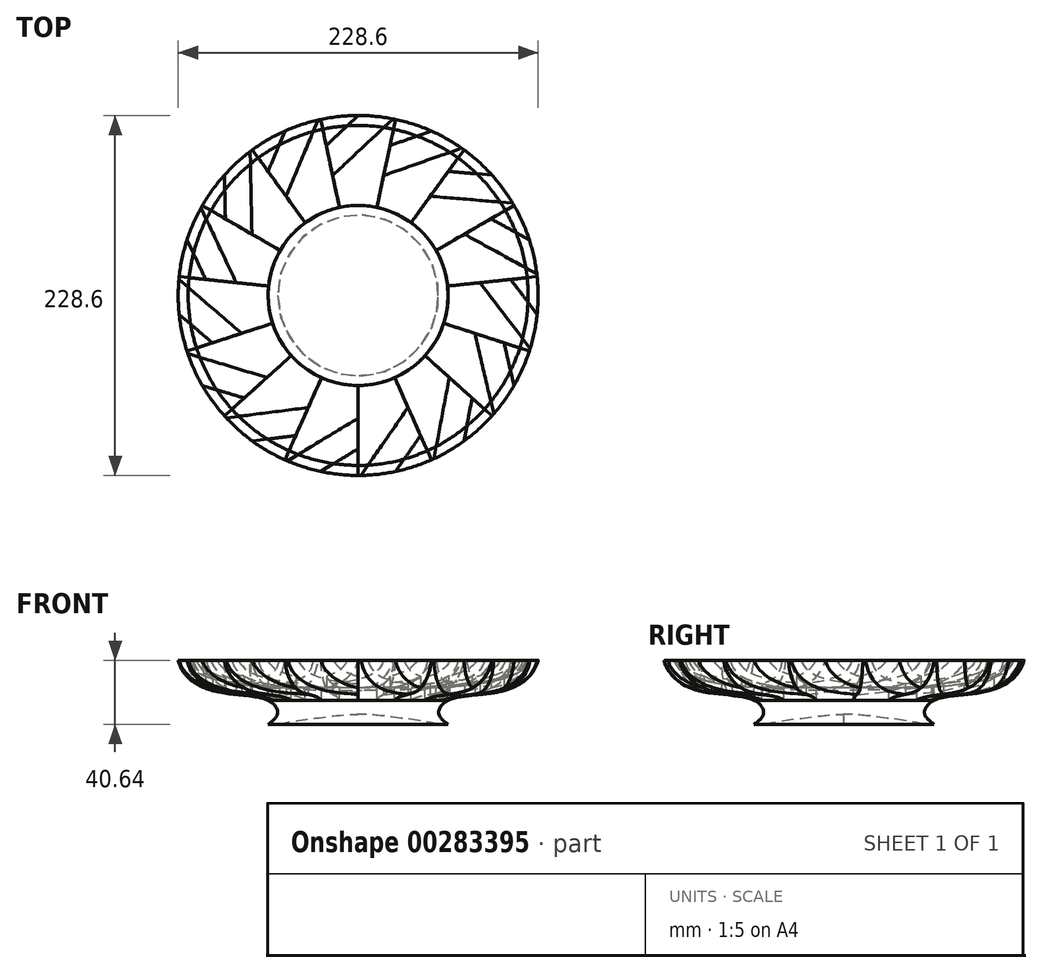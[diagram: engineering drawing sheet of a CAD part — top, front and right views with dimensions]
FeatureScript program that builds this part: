
annotation { "Feature Type Name" : "Feature", "Feature Type Description" : "" }
export const myFeature = defineFeature(function(context is Context, id is Id, definition is map)
    precondition{}
    {
        {
            var Q0;
            Q0=qCreatedBy(makeId("Top.planeOp"),FACE);
            var sketch = newSketch(context, id + "F0", { "sketchPlane" : qUnion([Q0])});
            skCircle(sketch, "E0", {"center": v(0, 0) * mm, "radius": 57.15 * mm});
            skLineSegment(sketch, "E1", {"start": v(0, 0) * mm, "end": v(0, 38.1) * mm, "construction": true});
            skLineSegment(sketch, "E2", {"start": v(0, 38.1) * mm, "end": v(0, 114.3) * mm, "construction": true});
            skCircle(sketch, "E3.cCircle", {"center": v(0, 0) * mm, "radius": 114.3 * mm, "construction": true});
            skLineSegment(sketch, "E3.0", {"start": v(-24.3, 114.3) * mm, "end": v(24.3, 114.3) * mm});
            skLineSegment(sketch, "E3.1", {"start": v(24.3, 114.3) * mm, "end": v(68.68, 94.54) * mm});
            skLineSegment(sketch, "E3.2", {"start": v(68.68, 94.54) * mm, "end": v(101.2, 58.43) * mm});
            skLineSegment(sketch, "E3.3", {"start": v(101.2, 58.43) * mm, "end": v(116.21, 12.21) * mm});
            skLineSegment(sketch, "E3.4", {"start": v(116.21, 12.21) * mm, "end": v(111.13, -36.1) * mm});
            skLineSegment(sketch, "E3.5", {"start": v(111.13, -36.1) * mm, "end": v(86.84, -78.2) * mm});
            skLineSegment(sketch, "E3.6", {"start": v(86.84, -78.2) * mm, "end": v(47.53, -106.75) * mm});
            skLineSegment(sketch, "E3.7", {"start": v(47.53, -106.75) * mm, "end": v(0, -116.85) * mm});
            skLineSegment(sketch, "E3.8", {"start": v(0, -116.85) * mm, "end": v(-47.53, -106.75) * mm});
            skLineSegment(sketch, "E3.9", {"start": v(-47.53, -106.75) * mm, "end": v(-86.84, -78.2) * mm});
            skLineSegment(sketch, "E3.10", {"start": v(-86.84, -78.2) * mm, "end": v(-111.13, -36.1) * mm});
            skLineSegment(sketch, "E3.11", {"start": v(-111.13, -36.1) * mm, "end": v(-116.21, 12.21) * mm});
            skLineSegment(sketch, "E3.12", {"start": v(-116.21, 12.21) * mm, "end": v(-101.2, 58.43) * mm});
            skLineSegment(sketch, "E3.13", {"start": v(-101.2, 58.43) * mm, "end": v(-68.68, 94.54) * mm});
            skLineSegment(sketch, "E3.14", {"start": v(-68.68, 94.54) * mm, "end": v(-24.3, 114.3) * mm});
            skPoint(sketch, "E3.0.midPoint", {"position": v(0, 114.3) * mm});
            skLineSegment(sketch, "E4", {"start": v(0, 0) * mm, "end": v(24.3, 114.3) * mm, "construction": true});
            skCircle(sketch, "E5.cCircle", {"center": v(0, 0) * mm, "radius": 38.95 * mm, "construction": true});
            skLineSegment(sketch, "E5.0", {"start": v(8.1, 38.1) * mm, "end": v(22.9, 31.51) * mm});
            skLineSegment(sketch, "E5.1", {"start": v(22.9, 31.51) * mm, "end": v(33.73, 19.48) * mm});
            skLineSegment(sketch, "E5.2", {"start": v(33.73, 19.48) * mm, "end": v(38.74, 4.07) * mm});
            skLineSegment(sketch, "E5.3", {"start": v(38.74, 4.07) * mm, "end": v(37.04, -12.04) * mm});
            skLineSegment(sketch, "E5.4", {"start": v(37.04, -12.04) * mm, "end": v(28.95, -26.06) * mm});
            skLineSegment(sketch, "E5.5", {"start": v(28.95, -26.06) * mm, "end": v(15.84, -35.58) * mm});
            skLineSegment(sketch, "E5.6", {"start": v(15.84, -35.58) * mm, "end": v(0, -38.95) * mm});
            skLineSegment(sketch, "E5.7", {"start": v(0, -38.95) * mm, "end": v(-15.84, -35.58) * mm});
            skLineSegment(sketch, "E5.8", {"start": v(-15.84, -35.58) * mm, "end": v(-28.95, -26.06) * mm});
            skLineSegment(sketch, "E5.9", {"start": v(-28.95, -26.06) * mm, "end": v(-37.04, -12.04) * mm});
            skLineSegment(sketch, "E5.10", {"start": v(-37.04, -12.04) * mm, "end": v(-38.74, 4.07) * mm});
            skLineSegment(sketch, "E5.11", {"start": v(-38.74, 4.07) * mm, "end": v(-33.73, 19.48) * mm});
            skLineSegment(sketch, "E5.12", {"start": v(-33.73, 19.48) * mm, "end": v(-22.9, 31.51) * mm});
            skLineSegment(sketch, "E5.13", {"start": v(-22.9, 31.51) * mm, "end": v(-8.1, 38.1) * mm});
            skLineSegment(sketch, "E5.14", {"start": v(-8.1, 38.1) * mm, "end": v(8.1, 38.1) * mm});
            skLineSegment(sketch, "E6", {"start": v(-22.9, 31.51) * mm, "end": v(-68.68, 94.54) * mm});
            skLineSegment(sketch, "E7", {"start": v(-24.3, 114.3) * mm, "end": v(-8.1, 38.1) * mm});
            skLineSegment(sketch, "E8", {"start": v(-24.3, 114.3) * mm, "end": v(-45.79, 63.02) * mm});
            skLineSegment(sketch, "E9", {"start": v(-46.49, 104.42) * mm, "end": v(-57.24, 78.78) * mm});
            skSolve(sketch);
        }
        {
            var Q0;
            Q0=makeQuery(id+"F0.imprint","IMPRINT",FACE,{"disambiguationData":[TD([[makeQuery(id+"F0.imprint","IMPRINT",EDGE,{"derivedFrom":sQuery(id+"F0.wireOp",EDGE,"E5.0")}),1.0]])]});
            var Q1;
            Q1=makeQuery(id+"F0.imprint","IMPRINT",FACE,{"disambiguationData":[TD([[makeQuery(id+"F0.imprint","IMPRINT",EDGE,{"derivedFrom":sQuery(id+"F0.wireOp",EDGE,"E5.0")}),-1.0]])]});
            var Q2;
            {var subQ5=sQuery(id+"F0.wireOp",EDGE,"E5.13");Q2=makeQuery(id+"F0.imprint","IMPRINT",FACE,{"disambiguationData":[TD([[makeQuery(id+"F0.imprint","IMPRINT",EDGE,{"derivedFrom":subQ5}),1.0]])]});}
            extrude(context, id + "F1", {"entities" : qUnion([Q0, Q1, Q2]), "oppositeDirection" : true, "depth" : 27.94 * mm});
        }
        {
            var Q0;
            {var subQ5=sQuery(id+"F0.wireOp",EDGE,"E8");Q0=makeQuery(id+"F0.imprint","IMPRINT",FACE,{"disambiguationData":[TD([[makeQuery(id+"F0.imprint","IMPRINT",EDGE,{"derivedFrom":subQ5}),1.0]])]});}
            var Q1;
            {var subQ5=sQuery(id+"F0.wireOp",EDGE,"E5.13");Q1=makeQuery(id+"F0.imprint","IMPRINT",FACE,{"disambiguationData":[TD([[makeQuery(id+"F0.imprint","IMPRINT",EDGE,{"derivedFrom":subQ5}),1.0]])]});}
            var Q2;
            {var subQ3=sQuery(id+"F0.wireOp",EDGE,"E9");Q2=makeQuery(id+"F0.imprint","IMPRINT",FACE,{"disambiguationData":[TD([[makeQuery(id+"F0.imprint","IMPRINT",EDGE,{"derivedFrom":subQ3}),-1.0]])]});}
            extrude(context, id + "F2", {"entities" : qUnion([Q0, Q1, Q2]), "depth" : 25.4 * mm});
        }
        {
            var Q0;
            {var subQ0=sQuery(id+"F0.wireOp",EDGE,"E8");Q0=makeQuery(id+"F0.imprint","IMPRINT",FACE,{"disambiguationData":[TD([[makeQuery(id+"F0.imprint","IMPRINT",EDGE,{"derivedFrom":subQ0}),-1.0]])]});}
            extrude(context, id + "F3", {"entities" : qUnion([Q0]), "depth" : 25.4 * mm});
        }
        {
            var Q0;
            Q0=makeQuery(id+"F2.opExtrude","SWEPT_BODY",BODY,{"disambiguationData":[OSD([sQuery(id+"F0.wireOp",EDGE,"E5.13"),sQuery(id+"F0.wireOp",EDGE,"E6"),sQuery(id+"F0.wireOp",EDGE,"E7"),sQuery(id+"F0.wireOp",EDGE,"E8")])]});
            var Q1;
            Q1=makeQuery(id+"F3.opExtrude","SWEPT_BODY",BODY,{"disambiguationData":[OSD([sQuery(id+"F0.wireOp",EDGE,"E3.14"),sQuery(id+"F0.wireOp",EDGE,"E6"),sQuery(id+"F0.wireOp",EDGE,"E8"),sQuery(id+"F0.wireOp",EDGE,"E9")])]});
            var Q2;
            Q2=makeQuery(id+"F2.opExtrude","SWEPT_BODY",BODY,{"disambiguationData":[OSD([sQuery(id+"F0.wireOp",EDGE,"E3.14"),sQuery(id+"F0.wireOp",EDGE,"E6"),sQuery(id+"F0.wireOp",EDGE,"E9")])]});
            transform(context, id + "F4", {"entities" : qUnion([Q0, Q1, Q2]), "transformType" : TransformType.TRANSLATION_3D, "dx" : 0 * mm, "dy" : 0 * mm, "dz" : -12.7 * mm, "makeCopy" : false});
        }
        {
            var Q0;
            Q0=makeQuery(id+"F1.opExtrude","SWEPT_BODY",BODY,{"disambiguationData":[OSD([sQuery(id+"F0.wireOp",EDGE,"E0")])]});
            var Q1;
            Q1=makeQuery(id+"F2.opExtrude","SWEPT_BODY",BODY,{"disambiguationData":[OSD([sQuery(id+"F0.wireOp",EDGE,"E5.13"),sQuery(id+"F0.wireOp",EDGE,"E6"),sQuery(id+"F0.wireOp",EDGE,"E7"),sQuery(id+"F0.wireOp",EDGE,"E8")])]});
            booleanBodies(context, id + "F5", {"operationType" : BooleanOperationType.SUBTRACTION, "tools" : qUnion([Q0]), "targets" : qUnion([Q1]), "keepTools" : true});
        }
        {
            var Q0;
            Q0=qCreatedBy(makeId("Right.planeOp"),FACE);
            var sketch = newSketch(context, id + "F6", { "sketchPlane" : qUnion([Q0])});
            skLineSegment(sketch, "E10", {"start": v(0, 0) * mm, "end": v(0, 114.3) * mm, "construction": true});
            skSolve(sketch);
        }
        {
            var Q0;
            Q0=makeQuery(id+"F2.opExtrude","SWEPT_BODY",BODY,{"disambiguationData":[OSD([sQuery(id+"F0.wireOp",EDGE,"E5.13"),sQuery(id+"F0.wireOp",EDGE,"E6"),sQuery(id+"F0.wireOp",EDGE,"E7"),sQuery(id+"F0.wireOp",EDGE,"E8")])]});
            var Q1;
            Q1=makeQuery(id+"F3.opExtrude","SWEPT_BODY",BODY,{"disambiguationData":[OSD([sQuery(id+"F0.wireOp",EDGE,"E3.14"),sQuery(id+"F0.wireOp",EDGE,"E6"),sQuery(id+"F0.wireOp",EDGE,"E8"),sQuery(id+"F0.wireOp",EDGE,"E9")])]});
            var Q2;
            Q2=makeQuery(id+"F2.opExtrude","SWEPT_BODY",BODY,{"disambiguationData":[OSD([sQuery(id+"F0.wireOp",EDGE,"E3.14"),sQuery(id+"F0.wireOp",EDGE,"E6"),sQuery(id+"F0.wireOp",EDGE,"E9")])]});
            var Q3;
            Q3=sQuery(id+"F6.wireOp",EDGE,"E10");
            transform(context, id + "F7", {"entities" : qUnion([Q0, Q1, Q2]), "transformType" : TransformType.ROTATION, "transformAxis" : qUnion([Q3]), "angle" : 24 * degree, "makeCopy" : true});
        }
        {
            var Q0;
            Q0=makeQuery(id+"F3.opExtrude","SWEPT_BODY",BODY,{"disambiguationData":[OSD([sQuery(id+"F0.wireOp",EDGE,"E3.14"),sQuery(id+"F0.wireOp",EDGE,"E6"),sQuery(id+"F0.wireOp",EDGE,"E8"),sQuery(id+"F0.wireOp",EDGE,"E9")])]});
            var Q1;
            Q1=makeQuery(id+"F2.opExtrude","SWEPT_BODY",BODY,{"disambiguationData":[OSD([sQuery(id+"F0.wireOp",EDGE,"E3.14"),sQuery(id+"F0.wireOp",EDGE,"E6"),sQuery(id+"F0.wireOp",EDGE,"E9")])]});
            var Q2;
            Q2=makeQuery(id+"F2.opExtrude","SWEPT_BODY",BODY,{"disambiguationData":[OSD([sQuery(id+"F0.wireOp",EDGE,"E5.13"),sQuery(id+"F0.wireOp",EDGE,"E6"),sQuery(id+"F0.wireOp",EDGE,"E7"),sQuery(id+"F0.wireOp",EDGE,"E8")])]});
            var Q3;
            Q3=makeQuery(id+"F7.opPattern","COPY",BODY,{"derivedFrom":makeQuery(id+"F3.opExtrude","SWEPT_BODY",BODY,{"disambiguationData":[OSD([sQuery(id+"F0.wireOp",EDGE,"E3.14"),sQuery(id+"F0.wireOp",EDGE,"E6"),sQuery(id+"F0.wireOp",EDGE,"E8"),sQuery(id+"F0.wireOp",EDGE,"E9")])]}),"instanceName":"1"});
            var Q4;
            Q4=makeQuery(id+"F7.opPattern","COPY",BODY,{"derivedFrom":makeQuery(id+"F2.opExtrude","SWEPT_BODY",BODY,{"disambiguationData":[OSD([sQuery(id+"F0.wireOp",EDGE,"E5.13"),sQuery(id+"F0.wireOp",EDGE,"E6"),sQuery(id+"F0.wireOp",EDGE,"E7"),sQuery(id+"F0.wireOp",EDGE,"E8")])]}),"instanceName":"1"});
            var Q5;
            Q5=makeQuery(id+"F7.opPattern","COPY",BODY,{"derivedFrom":makeQuery(id+"F2.opExtrude","SWEPT_BODY",BODY,{"disambiguationData":[OSD([sQuery(id+"F0.wireOp",EDGE,"E3.14"),sQuery(id+"F0.wireOp",EDGE,"E6"),sQuery(id+"F0.wireOp",EDGE,"E9")])]}),"instanceName":"1"});
            var Q6;
            Q6=sQuery(id+"F6.wireOp",EDGE,"E10");
            transform(context, id + "F8", {"entities" : qUnion([Q0, Q1, Q2, Q3, Q4, Q5]), "transformType" : TransformType.ROTATION, "transformAxis" : qUnion([Q6]), "angle" : 48 * degree, "makeCopy" : true});
        }
        {
            var Q0;
            Q0=makeQuery(id+"F8.opPattern","COPY",BODY,{"derivedFrom":makeQuery(id+"F7.opPattern","COPY",BODY,{"derivedFrom":makeQuery(id+"F2.opExtrude","SWEPT_BODY",BODY,{"disambiguationData":[OSD([sQuery(id+"F0.wireOp",EDGE,"E5.13"),sQuery(id+"F0.wireOp",EDGE,"E6"),sQuery(id+"F0.wireOp",EDGE,"E7"),sQuery(id+"F0.wireOp",EDGE,"E8")])]}),"instanceName":"1"}),"instanceName":"1"});
            var Q1;
            Q1=makeQuery(id+"F8.opPattern","COPY",BODY,{"derivedFrom":makeQuery(id+"F7.opPattern","COPY",BODY,{"derivedFrom":makeQuery(id+"F3.opExtrude","SWEPT_BODY",BODY,{"disambiguationData":[OSD([sQuery(id+"F0.wireOp",EDGE,"E3.14"),sQuery(id+"F0.wireOp",EDGE,"E6"),sQuery(id+"F0.wireOp",EDGE,"E8"),sQuery(id+"F0.wireOp",EDGE,"E9")])]}),"instanceName":"1"}),"instanceName":"1"});
            var Q2;
            Q2=makeQuery(id+"F8.opPattern","COPY",BODY,{"derivedFrom":makeQuery(id+"F7.opPattern","COPY",BODY,{"derivedFrom":makeQuery(id+"F2.opExtrude","SWEPT_BODY",BODY,{"disambiguationData":[OSD([sQuery(id+"F0.wireOp",EDGE,"E3.14"),sQuery(id+"F0.wireOp",EDGE,"E6"),sQuery(id+"F0.wireOp",EDGE,"E9")])]}),"instanceName":"1"}),"instanceName":"1"});
            var Q3;
            Q3=makeQuery(id+"F8.opPattern","COPY",BODY,{"derivedFrom":makeQuery(id+"F2.opExtrude","SWEPT_BODY",BODY,{"disambiguationData":[OSD([sQuery(id+"F0.wireOp",EDGE,"E3.14"),sQuery(id+"F0.wireOp",EDGE,"E6"),sQuery(id+"F0.wireOp",EDGE,"E9")])]}),"instanceName":"1"});
            var Q4;
            Q4=makeQuery(id+"F8.opPattern","COPY",BODY,{"derivedFrom":makeQuery(id+"F3.opExtrude","SWEPT_BODY",BODY,{"disambiguationData":[OSD([sQuery(id+"F0.wireOp",EDGE,"E3.14"),sQuery(id+"F0.wireOp",EDGE,"E6"),sQuery(id+"F0.wireOp",EDGE,"E8"),sQuery(id+"F0.wireOp",EDGE,"E9")])]}),"instanceName":"1"});
            var Q5;
            Q5=makeQuery(id+"F8.opPattern","COPY",BODY,{"derivedFrom":makeQuery(id+"F2.opExtrude","SWEPT_BODY",BODY,{"disambiguationData":[OSD([sQuery(id+"F0.wireOp",EDGE,"E5.13"),sQuery(id+"F0.wireOp",EDGE,"E6"),sQuery(id+"F0.wireOp",EDGE,"E7"),sQuery(id+"F0.wireOp",EDGE,"E8")])]}),"instanceName":"1"});
            var Q6;
            Q6=makeQuery(id+"F7.opPattern","COPY",BODY,{"derivedFrom":makeQuery(id+"F3.opExtrude","SWEPT_BODY",BODY,{"disambiguationData":[OSD([sQuery(id+"F0.wireOp",EDGE,"E3.14"),sQuery(id+"F0.wireOp",EDGE,"E6"),sQuery(id+"F0.wireOp",EDGE,"E8"),sQuery(id+"F0.wireOp",EDGE,"E9")])]}),"instanceName":"1"});
            var Q7;
            Q7=makeQuery(id+"F7.opPattern","COPY",BODY,{"derivedFrom":makeQuery(id+"F2.opExtrude","SWEPT_BODY",BODY,{"disambiguationData":[OSD([sQuery(id+"F0.wireOp",EDGE,"E3.14"),sQuery(id+"F0.wireOp",EDGE,"E6"),sQuery(id+"F0.wireOp",EDGE,"E9")])]}),"instanceName":"1"});
            var Q8;
            Q8=makeQuery(id+"F7.opPattern","COPY",BODY,{"derivedFrom":makeQuery(id+"F2.opExtrude","SWEPT_BODY",BODY,{"disambiguationData":[OSD([sQuery(id+"F0.wireOp",EDGE,"E5.13"),sQuery(id+"F0.wireOp",EDGE,"E6"),sQuery(id+"F0.wireOp",EDGE,"E7"),sQuery(id+"F0.wireOp",EDGE,"E8")])]}),"instanceName":"1"});
            var Q9;
            Q9=makeQuery(id+"F3.opExtrude","SWEPT_BODY",BODY,{"disambiguationData":[OSD([sQuery(id+"F0.wireOp",EDGE,"E3.14"),sQuery(id+"F0.wireOp",EDGE,"E6"),sQuery(id+"F0.wireOp",EDGE,"E8"),sQuery(id+"F0.wireOp",EDGE,"E9")])]});
            var Q10;
            Q10=makeQuery(id+"F2.opExtrude","SWEPT_BODY",BODY,{"disambiguationData":[OSD([sQuery(id+"F0.wireOp",EDGE,"E3.14"),sQuery(id+"F0.wireOp",EDGE,"E6"),sQuery(id+"F0.wireOp",EDGE,"E9")])]});
            var Q11;
            Q11=makeQuery(id+"F2.opExtrude","SWEPT_BODY",BODY,{"disambiguationData":[OSD([sQuery(id+"F0.wireOp",EDGE,"E5.13"),sQuery(id+"F0.wireOp",EDGE,"E6"),sQuery(id+"F0.wireOp",EDGE,"E7"),sQuery(id+"F0.wireOp",EDGE,"E8")])]});
            var Q12;
            Q12=sQuery(id+"F6.wireOp",EDGE,"E10");
            transform(context, id + "F9", {"entities" : qUnion([Q0, Q1, Q2, Q3, Q4, Q5, Q6, Q7, Q8, Q9, Q10, Q11]), "transformType" : TransformType.ROTATION, "transformAxis" : qUnion([Q12]), "angle" : 96 * degree, "makeCopy" : true});
        }
        {
            var Q0;
            Q0=makeQuery(id+"F7.opPattern","COPY",BODY,{"derivedFrom":makeQuery(id+"F2.opExtrude","SWEPT_BODY",BODY,{"disambiguationData":[OSD([sQuery(id+"F0.wireOp",EDGE,"E5.13"),sQuery(id+"F0.wireOp",EDGE,"E6"),sQuery(id+"F0.wireOp",EDGE,"E7"),sQuery(id+"F0.wireOp",EDGE,"E8")])]}),"instanceName":"1"});
            var Q1;
            Q1=makeQuery(id+"F7.opPattern","COPY",BODY,{"derivedFrom":makeQuery(id+"F3.opExtrude","SWEPT_BODY",BODY,{"disambiguationData":[OSD([sQuery(id+"F0.wireOp",EDGE,"E3.14"),sQuery(id+"F0.wireOp",EDGE,"E6"),sQuery(id+"F0.wireOp",EDGE,"E8"),sQuery(id+"F0.wireOp",EDGE,"E9")])]}),"instanceName":"1"});
            var Q2;
            Q2=makeQuery(id+"F7.opPattern","COPY",BODY,{"derivedFrom":makeQuery(id+"F2.opExtrude","SWEPT_BODY",BODY,{"disambiguationData":[OSD([sQuery(id+"F0.wireOp",EDGE,"E3.14"),sQuery(id+"F0.wireOp",EDGE,"E6"),sQuery(id+"F0.wireOp",EDGE,"E9")])]}),"instanceName":"1"});
            var Q3;
            Q3=makeQuery(id+"F8.opPattern","COPY",BODY,{"derivedFrom":makeQuery(id+"F2.opExtrude","SWEPT_BODY",BODY,{"disambiguationData":[OSD([sQuery(id+"F0.wireOp",EDGE,"E5.13"),sQuery(id+"F0.wireOp",EDGE,"E6"),sQuery(id+"F0.wireOp",EDGE,"E7"),sQuery(id+"F0.wireOp",EDGE,"E8")])]}),"instanceName":"1"});
            var Q4;
            Q4=makeQuery(id+"F8.opPattern","COPY",BODY,{"derivedFrom":makeQuery(id+"F3.opExtrude","SWEPT_BODY",BODY,{"disambiguationData":[OSD([sQuery(id+"F0.wireOp",EDGE,"E3.14"),sQuery(id+"F0.wireOp",EDGE,"E6"),sQuery(id+"F0.wireOp",EDGE,"E8"),sQuery(id+"F0.wireOp",EDGE,"E9")])]}),"instanceName":"1"});
            var Q5;
            Q5=makeQuery(id+"F8.opPattern","COPY",BODY,{"derivedFrom":makeQuery(id+"F2.opExtrude","SWEPT_BODY",BODY,{"disambiguationData":[OSD([sQuery(id+"F0.wireOp",EDGE,"E3.14"),sQuery(id+"F0.wireOp",EDGE,"E6"),sQuery(id+"F0.wireOp",EDGE,"E9")])]}),"instanceName":"1"});
            var Q6;
            Q6=makeQuery(id+"F8.opPattern","COPY",BODY,{"derivedFrom":makeQuery(id+"F7.opPattern","COPY",BODY,{"derivedFrom":makeQuery(id+"F2.opExtrude","SWEPT_BODY",BODY,{"disambiguationData":[OSD([sQuery(id+"F0.wireOp",EDGE,"E5.13"),sQuery(id+"F0.wireOp",EDGE,"E6"),sQuery(id+"F0.wireOp",EDGE,"E7"),sQuery(id+"F0.wireOp",EDGE,"E8")])]}),"instanceName":"1"}),"instanceName":"1"});
            var Q7;
            Q7=makeQuery(id+"F8.opPattern","COPY",BODY,{"derivedFrom":makeQuery(id+"F7.opPattern","COPY",BODY,{"derivedFrom":makeQuery(id+"F3.opExtrude","SWEPT_BODY",BODY,{"disambiguationData":[OSD([sQuery(id+"F0.wireOp",EDGE,"E3.14"),sQuery(id+"F0.wireOp",EDGE,"E6"),sQuery(id+"F0.wireOp",EDGE,"E8"),sQuery(id+"F0.wireOp",EDGE,"E9")])]}),"instanceName":"1"}),"instanceName":"1"});
            var Q8;
            Q8=makeQuery(id+"F8.opPattern","COPY",BODY,{"derivedFrom":makeQuery(id+"F7.opPattern","COPY",BODY,{"derivedFrom":makeQuery(id+"F2.opExtrude","SWEPT_BODY",BODY,{"disambiguationData":[OSD([sQuery(id+"F0.wireOp",EDGE,"E3.14"),sQuery(id+"F0.wireOp",EDGE,"E6"),sQuery(id+"F0.wireOp",EDGE,"E9")])]}),"instanceName":"1"}),"instanceName":"1"});
            var Q9;
            Q9=makeQuery(id+"F9.opPattern","COPY",BODY,{"derivedFrom":makeQuery(id+"F2.opExtrude","SWEPT_BODY",BODY,{"disambiguationData":[OSD([sQuery(id+"F0.wireOp",EDGE,"E5.13"),sQuery(id+"F0.wireOp",EDGE,"E6"),sQuery(id+"F0.wireOp",EDGE,"E7"),sQuery(id+"F0.wireOp",EDGE,"E8")])]}),"instanceName":"1"});
            var Q10;
            Q10=makeQuery(id+"F9.opPattern","COPY",BODY,{"derivedFrom":makeQuery(id+"F3.opExtrude","SWEPT_BODY",BODY,{"disambiguationData":[OSD([sQuery(id+"F0.wireOp",EDGE,"E3.14"),sQuery(id+"F0.wireOp",EDGE,"E6"),sQuery(id+"F0.wireOp",EDGE,"E8"),sQuery(id+"F0.wireOp",EDGE,"E9")])]}),"instanceName":"1"});
            var Q11;
            Q11=makeQuery(id+"F9.opPattern","COPY",BODY,{"derivedFrom":makeQuery(id+"F2.opExtrude","SWEPT_BODY",BODY,{"disambiguationData":[OSD([sQuery(id+"F0.wireOp",EDGE,"E3.14"),sQuery(id+"F0.wireOp",EDGE,"E6"),sQuery(id+"F0.wireOp",EDGE,"E9")])]}),"instanceName":"1"});
            var Q12;
            Q12=makeQuery(id+"F9.opPattern","COPY",BODY,{"derivedFrom":makeQuery(id+"F7.opPattern","COPY",BODY,{"derivedFrom":makeQuery(id+"F2.opExtrude","SWEPT_BODY",BODY,{"disambiguationData":[OSD([sQuery(id+"F0.wireOp",EDGE,"E5.13"),sQuery(id+"F0.wireOp",EDGE,"E6"),sQuery(id+"F0.wireOp",EDGE,"E7"),sQuery(id+"F0.wireOp",EDGE,"E8")])]}),"instanceName":"1"}),"instanceName":"1"});
            var Q13;
            Q13=makeQuery(id+"F9.opPattern","COPY",BODY,{"derivedFrom":makeQuery(id+"F7.opPattern","COPY",BODY,{"derivedFrom":makeQuery(id+"F3.opExtrude","SWEPT_BODY",BODY,{"disambiguationData":[OSD([sQuery(id+"F0.wireOp",EDGE,"E3.14"),sQuery(id+"F0.wireOp",EDGE,"E6"),sQuery(id+"F0.wireOp",EDGE,"E8"),sQuery(id+"F0.wireOp",EDGE,"E9")])]}),"instanceName":"1"}),"instanceName":"1"});
            var Q14;
            Q14=makeQuery(id+"F9.opPattern","COPY",BODY,{"derivedFrom":makeQuery(id+"F7.opPattern","COPY",BODY,{"derivedFrom":makeQuery(id+"F2.opExtrude","SWEPT_BODY",BODY,{"disambiguationData":[OSD([sQuery(id+"F0.wireOp",EDGE,"E3.14"),sQuery(id+"F0.wireOp",EDGE,"E6"),sQuery(id+"F0.wireOp",EDGE,"E9")])]}),"instanceName":"1"}),"instanceName":"1"});
            var Q15;
            Q15=makeQuery(id+"F9.opPattern","COPY",BODY,{"derivedFrom":makeQuery(id+"F8.opPattern","COPY",BODY,{"derivedFrom":makeQuery(id+"F2.opExtrude","SWEPT_BODY",BODY,{"disambiguationData":[OSD([sQuery(id+"F0.wireOp",EDGE,"E5.13"),sQuery(id+"F0.wireOp",EDGE,"E6"),sQuery(id+"F0.wireOp",EDGE,"E7"),sQuery(id+"F0.wireOp",EDGE,"E8")])]}),"instanceName":"1"}),"instanceName":"1"});
            var Q16;
            Q16=makeQuery(id+"F9.opPattern","COPY",BODY,{"derivedFrom":makeQuery(id+"F8.opPattern","COPY",BODY,{"derivedFrom":makeQuery(id+"F3.opExtrude","SWEPT_BODY",BODY,{"disambiguationData":[OSD([sQuery(id+"F0.wireOp",EDGE,"E3.14"),sQuery(id+"F0.wireOp",EDGE,"E6"),sQuery(id+"F0.wireOp",EDGE,"E8"),sQuery(id+"F0.wireOp",EDGE,"E9")])]}),"instanceName":"1"}),"instanceName":"1"});
            var Q17;
            Q17=makeQuery(id+"F9.opPattern","COPY",BODY,{"derivedFrom":makeQuery(id+"F8.opPattern","COPY",BODY,{"derivedFrom":makeQuery(id+"F2.opExtrude","SWEPT_BODY",BODY,{"disambiguationData":[OSD([sQuery(id+"F0.wireOp",EDGE,"E3.14"),sQuery(id+"F0.wireOp",EDGE,"E6"),sQuery(id+"F0.wireOp",EDGE,"E9")])]}),"instanceName":"1"}),"instanceName":"1"});
            var Q18;
            Q18=makeQuery(id+"F9.opPattern","COPY",BODY,{"derivedFrom":makeQuery(id+"F8.opPattern","COPY",BODY,{"derivedFrom":makeQuery(id+"F7.opPattern","COPY",BODY,{"derivedFrom":makeQuery(id+"F2.opExtrude","SWEPT_BODY",BODY,{"disambiguationData":[OSD([sQuery(id+"F0.wireOp",EDGE,"E5.13"),sQuery(id+"F0.wireOp",EDGE,"E6"),sQuery(id+"F0.wireOp",EDGE,"E7"),sQuery(id+"F0.wireOp",EDGE,"E8")])]}),"instanceName":"1"}),"instanceName":"1"}),"instanceName":"1"});
            var Q19;
            Q19=makeQuery(id+"F9.opPattern","COPY",BODY,{"derivedFrom":makeQuery(id+"F8.opPattern","COPY",BODY,{"derivedFrom":makeQuery(id+"F7.opPattern","COPY",BODY,{"derivedFrom":makeQuery(id+"F3.opExtrude","SWEPT_BODY",BODY,{"disambiguationData":[OSD([sQuery(id+"F0.wireOp",EDGE,"E3.14"),sQuery(id+"F0.wireOp",EDGE,"E6"),sQuery(id+"F0.wireOp",EDGE,"E8"),sQuery(id+"F0.wireOp",EDGE,"E9")])]}),"instanceName":"1"}),"instanceName":"1"}),"instanceName":"1"});
            var Q20;
            Q20=makeQuery(id+"F9.opPattern","COPY",BODY,{"derivedFrom":makeQuery(id+"F8.opPattern","COPY",BODY,{"derivedFrom":makeQuery(id+"F7.opPattern","COPY",BODY,{"derivedFrom":makeQuery(id+"F2.opExtrude","SWEPT_BODY",BODY,{"disambiguationData":[OSD([sQuery(id+"F0.wireOp",EDGE,"E3.14"),sQuery(id+"F0.wireOp",EDGE,"E6"),sQuery(id+"F0.wireOp",EDGE,"E9")])]}),"instanceName":"1"}),"instanceName":"1"}),"instanceName":"1"});
            var Q21;
            Q21=sQuery(id+"F6.wireOp",EDGE,"E10");
            transform(context, id + "F10", {"entities" : qUnion([Q0, Q1, Q2, Q3, Q4, Q5, Q6, Q7, Q8, Q9, Q10, Q11, Q12, Q13, Q14, Q15, Q16, Q17, Q18, Q19, Q20]), "transformType" : TransformType.ROTATION, "transformAxis" : qUnion([Q21]), "angle" : 168 * degree, "makeCopy" : true});
        }
        {
            var Q0;
            Q0=qCreatedBy(makeId("Front.planeOp"),FACE);
            var sketch = newSketch(context, id + "F11", { "sketchPlane" : qUnion([Q0])});
            skLineSegment(sketch, "E11", {"start": v(0, 0) * mm, "end": v(0, -27.94) * mm});
            skLineSegment(sketch, "E12", {"start": v(0, -27.94) * mm, "end": v(-57.15, -27.94) * mm, "construction": true});
            skLineSegment(sketch, "E13", {"start": v(-57.15, -27.94) * mm, "end": v(-57.15, -12.7) * mm, "construction": true});
            skLineSegment(sketch, "E14", {"start": v(-57.15, -12.7) * mm, "end": v(-114.3, -12.7) * mm, "construction": true});
            skLineSegment(sketch, "E15", {"start": v(-114.3, -12.7) * mm, "end": v(-114.3, 12.7) * mm, "construction": true});
            skLineSegment(sketch, "E16", {"start": v(-114.3, 12.7) * mm, "end": v(-43.18, 12.7) * mm, "construction": true});
            skFitSpline(sketch, "E17", {"points": [v(-57.15, -27.94) * mm, v(-51.17, -21.25) * mm, v(-57.15, -12.7) * mm, v(-92.77, -6.44) * mm, v(-114.3, 12.7) * mm], "startDerivative": vector(47.9, 35.87) * mm, "endDerivative": vector(-23.78, 94.45) * mm});
            skLineSegment(sketch, "E18", {"start": v(-114.3, 12.7) * mm, "end": v(-107.95, 12.7) * mm});
            skLineSegment(sketch, "E19", {"start": v(0, 0) * mm, "end": v(0, -6.35) * mm, "construction": true});
            skFitSpline(sketch, "E20", {"points": [v(-107.95, 12.7) * mm, v(-95.05, 1.75) * mm, v(-41.56, -5.41) * mm, v(0, -6.35) * mm], "startDerivative": vector(24, -66.96) * mm, "endDerivative": vector(129.34, -1.24) * mm});
            skLineSegment(sketch, "E21", {"start": v(0, -6.35) * mm, "end": v(0, -27.94) * mm});
            skLineSegment(sketch, "E22", {"start": v(0, -27.94) * mm, "end": v(0, -21.6) * mm, "construction": true});
            skLineSegment(sketch, "E23", {"start": v(-57.15, -27.94) * mm, "end": v(-50.8, -27.94) * mm});
            skFitSpline(sketch, "E24", {"points": [v(-50.8, -27.94) * mm, v(-26.3, -23.89) * mm, v(0, -21.6) * mm], "startDerivative": vector(49.3, 13.08) * mm, "endDerivative": vector(52.28, -0.34) * mm});
            skSolve(sketch);
        }
        {
            var Q0;
            Q0 = qSketchRegion(id + "F11", true);
            var Q1;
            Q1=sQuery(id+"F6.wireOp",EDGE,"E10");
            revolve(context, id + "F12", {"entities" : qUnion([Q0]), "axis" : qUnion([Q1]), "revolveType" : RevolveType.FULL});
        }
        {
            var Q0;
            Q0=makeQuery(id+"F1.opExtrude","CAP_FACE",FACE,{"disambiguationData":[OSD([sQuery(id+"F0.wireOp",EDGE,"E0")])],"isStart":false});
            var sketch = newSketch(context, id + "F13", { "sketchPlane" : qUnion([Q0])});
            skCircle(sketch, "E25", {"center": v(0, 0) * mm, "radius": 127 * mm});
            skSolve(sketch);
        }
        {
            var Q0;
            Q0=makeQuery(id+"F13.imprint","IMPRINT",FACE,{"disambiguationData":[TD([[makeQuery(id+"F13.imprint","IMPRINT",EDGE,{"derivedFrom":sQuery(id+"F13.wireOp",EDGE,"E25")}),1.0]])]});
            var Q1;
            Q1=makeQuery(id+"F13.imprint","IMPRINT",FACE,{"disambiguationData":[TD([[makeQuery(id+"F13.imprint","IMPRINT",EDGE,{"derivedFrom":makeQuery(id+"F1.opExtrude","CAP_EDGE",EDGE,{"disambiguationData":[OSD([sQuery(id+"F0.wireOp",EDGE,"E0")])],"isStart":false})}),-1.0]])]});
            extrude(context, id + "F14", {"entities" : qUnion([Q0, Q1]), "oppositeDirection" : true, "depth" : 40.64 * mm});
        }
        {
            var Q0;
            Q0=makeQuery(id+"F12.opRevolve","SWEPT_BODY",BODY,{"disambiguationData":[OSD([sQuery(id+"F11.wireOp",EDGE,"E17"),sQuery(id+"F11.wireOp",EDGE,"E18"),sQuery(id+"F11.wireOp",EDGE,"E20"),sQuery(id+"F11.wireOp",EDGE,"E21"),sQuery(id+"F11.wireOp",EDGE,"E23"),sQuery(id+"F11.wireOp",EDGE,"E24")])]});
            var Q1;
            Q1=makeQuery(id+"F14.opExtrude","SWEPT_BODY",BODY,{"disambiguationData":[OSD([sQuery(id+"F13.wireOp",EDGE,"E25")])]});
            booleanBodies(context, id + "F15", {"operationType" : BooleanOperationType.SUBTRACTION, "tools" : qUnion([Q0]), "targets" : qUnion([Q1])});
        }
        {
            var Q0;
            Q0=makeQuery(id+"F15.opBoolean","SPLIT",BODY,{"disambiguationData":[OD(2.0)],"derivedFrom":makeQuery(id+"F14.opExtrude","SWEPT_BODY",BODY,{"disambiguationData":[OSD([sQuery(id+"F13.wireOp",EDGE,"E25")])]})});
            var Q1;
            Q1=makeQuery(id+"F15.opBoolean","SPLIT",BODY,{"disambiguationData":[OD(0.0)],"derivedFrom":makeQuery(id+"F14.opExtrude","SWEPT_BODY",BODY,{"disambiguationData":[OSD([sQuery(id+"F13.wireOp",EDGE,"E25")])]})});
            var Q2;
            Q2=makeQuery(id+"F15.opBoolean","SPLIT",BODY,{"disambiguationData":[OD(1.0)],"derivedFrom":makeQuery(id+"F14.opExtrude","SWEPT_BODY",BODY,{"disambiguationData":[OSD([sQuery(id+"F13.wireOp",EDGE,"E25")])]})});
            var Q3;
            Q3=makeQuery(id+"F10.opPattern","COPY",BODY,{"derivedFrom":makeQuery(id+"F9.opPattern","COPY",BODY,{"derivedFrom":makeQuery(id+"F8.opPattern","COPY",BODY,{"derivedFrom":makeQuery(id+"F7.opPattern","COPY",BODY,{"derivedFrom":makeQuery(id+"F3.opExtrude","SWEPT_BODY",BODY,{"disambiguationData":[OSD([sQuery(id+"F0.wireOp",EDGE,"E3.14"),sQuery(id+"F0.wireOp",EDGE,"E6"),sQuery(id+"F0.wireOp",EDGE,"E8"),sQuery(id+"F0.wireOp",EDGE,"E9")])]}),"instanceName":"1"}),"instanceName":"1"}),"instanceName":"1"}),"instanceName":"1"});
            var Q4;
            Q4=makeQuery(id+"F1.opExtrude","SWEPT_BODY",BODY,{"disambiguationData":[OSD([sQuery(id+"F0.wireOp",EDGE,"E0")])]});
            var Q5;
            Q5=makeQuery(id+"F2.opExtrude","SWEPT_BODY",BODY,{"disambiguationData":[OSD([sQuery(id+"F0.wireOp",EDGE,"E3.14"),sQuery(id+"F0.wireOp",EDGE,"E6"),sQuery(id+"F0.wireOp",EDGE,"E9")])]});
            var Q6;
            Q6=makeQuery(id+"F2.opExtrude","SWEPT_BODY",BODY,{"disambiguationData":[OSD([sQuery(id+"F0.wireOp",EDGE,"E5.13"),sQuery(id+"F0.wireOp",EDGE,"E6"),sQuery(id+"F0.wireOp",EDGE,"E7"),sQuery(id+"F0.wireOp",EDGE,"E8")])]});
            var Q7;
            Q7=makeQuery(id+"F3.opExtrude","SWEPT_BODY",BODY,{"disambiguationData":[OSD([sQuery(id+"F0.wireOp",EDGE,"E3.14"),sQuery(id+"F0.wireOp",EDGE,"E6"),sQuery(id+"F0.wireOp",EDGE,"E8"),sQuery(id+"F0.wireOp",EDGE,"E9")])]});
            var Q8;
            Q8=makeQuery(id+"F7.opPattern","COPY",BODY,{"derivedFrom":makeQuery(id+"F2.opExtrude","SWEPT_BODY",BODY,{"disambiguationData":[OSD([sQuery(id+"F0.wireOp",EDGE,"E3.14"),sQuery(id+"F0.wireOp",EDGE,"E6"),sQuery(id+"F0.wireOp",EDGE,"E9")])]}),"instanceName":"1"});
            var Q9;
            Q9=makeQuery(id+"F7.opPattern","COPY",BODY,{"derivedFrom":makeQuery(id+"F2.opExtrude","SWEPT_BODY",BODY,{"disambiguationData":[OSD([sQuery(id+"F0.wireOp",EDGE,"E5.13"),sQuery(id+"F0.wireOp",EDGE,"E6"),sQuery(id+"F0.wireOp",EDGE,"E7"),sQuery(id+"F0.wireOp",EDGE,"E8")])]}),"instanceName":"1"});
            var Q10;
            Q10=makeQuery(id+"F7.opPattern","COPY",BODY,{"derivedFrom":makeQuery(id+"F3.opExtrude","SWEPT_BODY",BODY,{"disambiguationData":[OSD([sQuery(id+"F0.wireOp",EDGE,"E3.14"),sQuery(id+"F0.wireOp",EDGE,"E6"),sQuery(id+"F0.wireOp",EDGE,"E8"),sQuery(id+"F0.wireOp",EDGE,"E9")])]}),"instanceName":"1"});
            var Q11;
            Q11=makeQuery(id+"F8.opPattern","COPY",BODY,{"derivedFrom":makeQuery(id+"F2.opExtrude","SWEPT_BODY",BODY,{"disambiguationData":[OSD([sQuery(id+"F0.wireOp",EDGE,"E3.14"),sQuery(id+"F0.wireOp",EDGE,"E6"),sQuery(id+"F0.wireOp",EDGE,"E9")])]}),"instanceName":"1"});
            var Q12;
            Q12=makeQuery(id+"F8.opPattern","COPY",BODY,{"derivedFrom":makeQuery(id+"F2.opExtrude","SWEPT_BODY",BODY,{"disambiguationData":[OSD([sQuery(id+"F0.wireOp",EDGE,"E5.13"),sQuery(id+"F0.wireOp",EDGE,"E6"),sQuery(id+"F0.wireOp",EDGE,"E7"),sQuery(id+"F0.wireOp",EDGE,"E8")])]}),"instanceName":"1"});
            var Q13;
            Q13=makeQuery(id+"F8.opPattern","COPY",BODY,{"derivedFrom":makeQuery(id+"F3.opExtrude","SWEPT_BODY",BODY,{"disambiguationData":[OSD([sQuery(id+"F0.wireOp",EDGE,"E3.14"),sQuery(id+"F0.wireOp",EDGE,"E6"),sQuery(id+"F0.wireOp",EDGE,"E8"),sQuery(id+"F0.wireOp",EDGE,"E9")])]}),"instanceName":"1"});
            var Q14;
            Q14=makeQuery(id+"F8.opPattern","COPY",BODY,{"derivedFrom":makeQuery(id+"F7.opPattern","COPY",BODY,{"derivedFrom":makeQuery(id+"F2.opExtrude","SWEPT_BODY",BODY,{"disambiguationData":[OSD([sQuery(id+"F0.wireOp",EDGE,"E3.14"),sQuery(id+"F0.wireOp",EDGE,"E6"),sQuery(id+"F0.wireOp",EDGE,"E9")])]}),"instanceName":"1"}),"instanceName":"1"});
            var Q15;
            Q15=makeQuery(id+"F8.opPattern","COPY",BODY,{"derivedFrom":makeQuery(id+"F7.opPattern","COPY",BODY,{"derivedFrom":makeQuery(id+"F2.opExtrude","SWEPT_BODY",BODY,{"disambiguationData":[OSD([sQuery(id+"F0.wireOp",EDGE,"E5.13"),sQuery(id+"F0.wireOp",EDGE,"E6"),sQuery(id+"F0.wireOp",EDGE,"E7"),sQuery(id+"F0.wireOp",EDGE,"E8")])]}),"instanceName":"1"}),"instanceName":"1"});
            var Q16;
            Q16=makeQuery(id+"F8.opPattern","COPY",BODY,{"derivedFrom":makeQuery(id+"F7.opPattern","COPY",BODY,{"derivedFrom":makeQuery(id+"F3.opExtrude","SWEPT_BODY",BODY,{"disambiguationData":[OSD([sQuery(id+"F0.wireOp",EDGE,"E3.14"),sQuery(id+"F0.wireOp",EDGE,"E6"),sQuery(id+"F0.wireOp",EDGE,"E8"),sQuery(id+"F0.wireOp",EDGE,"E9")])]}),"instanceName":"1"}),"instanceName":"1"});
            var Q17;
            Q17=makeQuery(id+"F9.opPattern","COPY",BODY,{"derivedFrom":makeQuery(id+"F2.opExtrude","SWEPT_BODY",BODY,{"disambiguationData":[OSD([sQuery(id+"F0.wireOp",EDGE,"E3.14"),sQuery(id+"F0.wireOp",EDGE,"E6"),sQuery(id+"F0.wireOp",EDGE,"E9")])]}),"instanceName":"1"});
            var Q18;
            Q18=makeQuery(id+"F9.opPattern","COPY",BODY,{"derivedFrom":makeQuery(id+"F2.opExtrude","SWEPT_BODY",BODY,{"disambiguationData":[OSD([sQuery(id+"F0.wireOp",EDGE,"E5.13"),sQuery(id+"F0.wireOp",EDGE,"E6"),sQuery(id+"F0.wireOp",EDGE,"E7"),sQuery(id+"F0.wireOp",EDGE,"E8")])]}),"instanceName":"1"});
            var Q19;
            Q19=makeQuery(id+"F9.opPattern","COPY",BODY,{"derivedFrom":makeQuery(id+"F3.opExtrude","SWEPT_BODY",BODY,{"disambiguationData":[OSD([sQuery(id+"F0.wireOp",EDGE,"E3.14"),sQuery(id+"F0.wireOp",EDGE,"E6"),sQuery(id+"F0.wireOp",EDGE,"E8"),sQuery(id+"F0.wireOp",EDGE,"E9")])]}),"instanceName":"1"});
            var Q20;
            Q20=makeQuery(id+"F9.opPattern","COPY",BODY,{"derivedFrom":makeQuery(id+"F7.opPattern","COPY",BODY,{"derivedFrom":makeQuery(id+"F2.opExtrude","SWEPT_BODY",BODY,{"disambiguationData":[OSD([sQuery(id+"F0.wireOp",EDGE,"E3.14"),sQuery(id+"F0.wireOp",EDGE,"E6"),sQuery(id+"F0.wireOp",EDGE,"E9")])]}),"instanceName":"1"}),"instanceName":"1"});
            var Q21;
            Q21=makeQuery(id+"F9.opPattern","COPY",BODY,{"derivedFrom":makeQuery(id+"F7.opPattern","COPY",BODY,{"derivedFrom":makeQuery(id+"F2.opExtrude","SWEPT_BODY",BODY,{"disambiguationData":[OSD([sQuery(id+"F0.wireOp",EDGE,"E5.13"),sQuery(id+"F0.wireOp",EDGE,"E6"),sQuery(id+"F0.wireOp",EDGE,"E7"),sQuery(id+"F0.wireOp",EDGE,"E8")])]}),"instanceName":"1"}),"instanceName":"1"});
            var Q22;
            Q22=makeQuery(id+"F9.opPattern","COPY",BODY,{"derivedFrom":makeQuery(id+"F7.opPattern","COPY",BODY,{"derivedFrom":makeQuery(id+"F3.opExtrude","SWEPT_BODY",BODY,{"disambiguationData":[OSD([sQuery(id+"F0.wireOp",EDGE,"E3.14"),sQuery(id+"F0.wireOp",EDGE,"E6"),sQuery(id+"F0.wireOp",EDGE,"E8"),sQuery(id+"F0.wireOp",EDGE,"E9")])]}),"instanceName":"1"}),"instanceName":"1"});
            var Q23;
            Q23=makeQuery(id+"F9.opPattern","COPY",BODY,{"derivedFrom":makeQuery(id+"F8.opPattern","COPY",BODY,{"derivedFrom":makeQuery(id+"F2.opExtrude","SWEPT_BODY",BODY,{"disambiguationData":[OSD([sQuery(id+"F0.wireOp",EDGE,"E3.14"),sQuery(id+"F0.wireOp",EDGE,"E6"),sQuery(id+"F0.wireOp",EDGE,"E9")])]}),"instanceName":"1"}),"instanceName":"1"});
            var Q24;
            Q24=makeQuery(id+"F9.opPattern","COPY",BODY,{"derivedFrom":makeQuery(id+"F8.opPattern","COPY",BODY,{"derivedFrom":makeQuery(id+"F2.opExtrude","SWEPT_BODY",BODY,{"disambiguationData":[OSD([sQuery(id+"F0.wireOp",EDGE,"E5.13"),sQuery(id+"F0.wireOp",EDGE,"E6"),sQuery(id+"F0.wireOp",EDGE,"E7"),sQuery(id+"F0.wireOp",EDGE,"E8")])]}),"instanceName":"1"}),"instanceName":"1"});
            var Q25;
            Q25=makeQuery(id+"F9.opPattern","COPY",BODY,{"derivedFrom":makeQuery(id+"F8.opPattern","COPY",BODY,{"derivedFrom":makeQuery(id+"F3.opExtrude","SWEPT_BODY",BODY,{"disambiguationData":[OSD([sQuery(id+"F0.wireOp",EDGE,"E3.14"),sQuery(id+"F0.wireOp",EDGE,"E6"),sQuery(id+"F0.wireOp",EDGE,"E8"),sQuery(id+"F0.wireOp",EDGE,"E9")])]}),"instanceName":"1"}),"instanceName":"1"});
            var Q26;
            Q26=makeQuery(id+"F9.opPattern","COPY",BODY,{"derivedFrom":makeQuery(id+"F8.opPattern","COPY",BODY,{"derivedFrom":makeQuery(id+"F7.opPattern","COPY",BODY,{"derivedFrom":makeQuery(id+"F2.opExtrude","SWEPT_BODY",BODY,{"disambiguationData":[OSD([sQuery(id+"F0.wireOp",EDGE,"E3.14"),sQuery(id+"F0.wireOp",EDGE,"E6"),sQuery(id+"F0.wireOp",EDGE,"E9")])]}),"instanceName":"1"}),"instanceName":"1"}),"instanceName":"1"});
            var Q27;
            Q27=makeQuery(id+"F9.opPattern","COPY",BODY,{"derivedFrom":makeQuery(id+"F8.opPattern","COPY",BODY,{"derivedFrom":makeQuery(id+"F7.opPattern","COPY",BODY,{"derivedFrom":makeQuery(id+"F2.opExtrude","SWEPT_BODY",BODY,{"disambiguationData":[OSD([sQuery(id+"F0.wireOp",EDGE,"E5.13"),sQuery(id+"F0.wireOp",EDGE,"E6"),sQuery(id+"F0.wireOp",EDGE,"E7"),sQuery(id+"F0.wireOp",EDGE,"E8")])]}),"instanceName":"1"}),"instanceName":"1"}),"instanceName":"1"});
            var Q28;
            Q28=makeQuery(id+"F9.opPattern","COPY",BODY,{"derivedFrom":makeQuery(id+"F8.opPattern","COPY",BODY,{"derivedFrom":makeQuery(id+"F7.opPattern","COPY",BODY,{"derivedFrom":makeQuery(id+"F3.opExtrude","SWEPT_BODY",BODY,{"disambiguationData":[OSD([sQuery(id+"F0.wireOp",EDGE,"E3.14"),sQuery(id+"F0.wireOp",EDGE,"E6"),sQuery(id+"F0.wireOp",EDGE,"E8"),sQuery(id+"F0.wireOp",EDGE,"E9")])]}),"instanceName":"1"}),"instanceName":"1"}),"instanceName":"1"});
            var Q29;
            Q29=makeQuery(id+"F10.opPattern","COPY",BODY,{"derivedFrom":makeQuery(id+"F7.opPattern","COPY",BODY,{"derivedFrom":makeQuery(id+"F2.opExtrude","SWEPT_BODY",BODY,{"disambiguationData":[OSD([sQuery(id+"F0.wireOp",EDGE,"E3.14"),sQuery(id+"F0.wireOp",EDGE,"E6"),sQuery(id+"F0.wireOp",EDGE,"E9")])]}),"instanceName":"1"}),"instanceName":"1"});
            var Q30;
            Q30=makeQuery(id+"F10.opPattern","COPY",BODY,{"derivedFrom":makeQuery(id+"F7.opPattern","COPY",BODY,{"derivedFrom":makeQuery(id+"F2.opExtrude","SWEPT_BODY",BODY,{"disambiguationData":[OSD([sQuery(id+"F0.wireOp",EDGE,"E5.13"),sQuery(id+"F0.wireOp",EDGE,"E6"),sQuery(id+"F0.wireOp",EDGE,"E7"),sQuery(id+"F0.wireOp",EDGE,"E8")])]}),"instanceName":"1"}),"instanceName":"1"});
            var Q31;
            Q31=makeQuery(id+"F10.opPattern","COPY",BODY,{"derivedFrom":makeQuery(id+"F7.opPattern","COPY",BODY,{"derivedFrom":makeQuery(id+"F3.opExtrude","SWEPT_BODY",BODY,{"disambiguationData":[OSD([sQuery(id+"F0.wireOp",EDGE,"E3.14"),sQuery(id+"F0.wireOp",EDGE,"E6"),sQuery(id+"F0.wireOp",EDGE,"E8"),sQuery(id+"F0.wireOp",EDGE,"E9")])]}),"instanceName":"1"}),"instanceName":"1"});
            var Q32;
            Q32=makeQuery(id+"F10.opPattern","COPY",BODY,{"derivedFrom":makeQuery(id+"F8.opPattern","COPY",BODY,{"derivedFrom":makeQuery(id+"F2.opExtrude","SWEPT_BODY",BODY,{"disambiguationData":[OSD([sQuery(id+"F0.wireOp",EDGE,"E3.14"),sQuery(id+"F0.wireOp",EDGE,"E6"),sQuery(id+"F0.wireOp",EDGE,"E9")])]}),"instanceName":"1"}),"instanceName":"1"});
            var Q33;
            Q33=makeQuery(id+"F10.opPattern","COPY",BODY,{"derivedFrom":makeQuery(id+"F8.opPattern","COPY",BODY,{"derivedFrom":makeQuery(id+"F2.opExtrude","SWEPT_BODY",BODY,{"disambiguationData":[OSD([sQuery(id+"F0.wireOp",EDGE,"E5.13"),sQuery(id+"F0.wireOp",EDGE,"E6"),sQuery(id+"F0.wireOp",EDGE,"E7"),sQuery(id+"F0.wireOp",EDGE,"E8")])]}),"instanceName":"1"}),"instanceName":"1"});
            var Q34;
            Q34=makeQuery(id+"F10.opPattern","COPY",BODY,{"derivedFrom":makeQuery(id+"F8.opPattern","COPY",BODY,{"derivedFrom":makeQuery(id+"F3.opExtrude","SWEPT_BODY",BODY,{"disambiguationData":[OSD([sQuery(id+"F0.wireOp",EDGE,"E3.14"),sQuery(id+"F0.wireOp",EDGE,"E6"),sQuery(id+"F0.wireOp",EDGE,"E8"),sQuery(id+"F0.wireOp",EDGE,"E9")])]}),"instanceName":"1"}),"instanceName":"1"});
            var Q35;
            Q35=makeQuery(id+"F10.opPattern","COPY",BODY,{"derivedFrom":makeQuery(id+"F8.opPattern","COPY",BODY,{"derivedFrom":makeQuery(id+"F7.opPattern","COPY",BODY,{"derivedFrom":makeQuery(id+"F2.opExtrude","SWEPT_BODY",BODY,{"disambiguationData":[OSD([sQuery(id+"F0.wireOp",EDGE,"E3.14"),sQuery(id+"F0.wireOp",EDGE,"E6"),sQuery(id+"F0.wireOp",EDGE,"E9")])]}),"instanceName":"1"}),"instanceName":"1"}),"instanceName":"1"});
            var Q36;
            Q36=makeQuery(id+"F10.opPattern","COPY",BODY,{"derivedFrom":makeQuery(id+"F8.opPattern","COPY",BODY,{"derivedFrom":makeQuery(id+"F7.opPattern","COPY",BODY,{"derivedFrom":makeQuery(id+"F2.opExtrude","SWEPT_BODY",BODY,{"disambiguationData":[OSD([sQuery(id+"F0.wireOp",EDGE,"E5.13"),sQuery(id+"F0.wireOp",EDGE,"E6"),sQuery(id+"F0.wireOp",EDGE,"E7"),sQuery(id+"F0.wireOp",EDGE,"E8")])]}),"instanceName":"1"}),"instanceName":"1"}),"instanceName":"1"});
            var Q37;
            Q37=makeQuery(id+"F10.opPattern","COPY",BODY,{"derivedFrom":makeQuery(id+"F8.opPattern","COPY",BODY,{"derivedFrom":makeQuery(id+"F7.opPattern","COPY",BODY,{"derivedFrom":makeQuery(id+"F3.opExtrude","SWEPT_BODY",BODY,{"disambiguationData":[OSD([sQuery(id+"F0.wireOp",EDGE,"E3.14"),sQuery(id+"F0.wireOp",EDGE,"E6"),sQuery(id+"F0.wireOp",EDGE,"E8"),sQuery(id+"F0.wireOp",EDGE,"E9")])]}),"instanceName":"1"}),"instanceName":"1"}),"instanceName":"1"});
            var Q38;
            Q38=makeQuery(id+"F10.opPattern","COPY",BODY,{"derivedFrom":makeQuery(id+"F9.opPattern","COPY",BODY,{"derivedFrom":makeQuery(id+"F2.opExtrude","SWEPT_BODY",BODY,{"disambiguationData":[OSD([sQuery(id+"F0.wireOp",EDGE,"E3.14"),sQuery(id+"F0.wireOp",EDGE,"E6"),sQuery(id+"F0.wireOp",EDGE,"E9")])]}),"instanceName":"1"}),"instanceName":"1"});
            var Q39;
            Q39=makeQuery(id+"F10.opPattern","COPY",BODY,{"derivedFrom":makeQuery(id+"F9.opPattern","COPY",BODY,{"derivedFrom":makeQuery(id+"F2.opExtrude","SWEPT_BODY",BODY,{"disambiguationData":[OSD([sQuery(id+"F0.wireOp",EDGE,"E5.13"),sQuery(id+"F0.wireOp",EDGE,"E6"),sQuery(id+"F0.wireOp",EDGE,"E7"),sQuery(id+"F0.wireOp",EDGE,"E8")])]}),"instanceName":"1"}),"instanceName":"1"});
            var Q40;
            Q40=makeQuery(id+"F10.opPattern","COPY",BODY,{"derivedFrom":makeQuery(id+"F9.opPattern","COPY",BODY,{"derivedFrom":makeQuery(id+"F3.opExtrude","SWEPT_BODY",BODY,{"disambiguationData":[OSD([sQuery(id+"F0.wireOp",EDGE,"E3.14"),sQuery(id+"F0.wireOp",EDGE,"E6"),sQuery(id+"F0.wireOp",EDGE,"E8"),sQuery(id+"F0.wireOp",EDGE,"E9")])]}),"instanceName":"1"}),"instanceName":"1"});
            var Q41;
            Q41=makeQuery(id+"F10.opPattern","COPY",BODY,{"derivedFrom":makeQuery(id+"F9.opPattern","COPY",BODY,{"derivedFrom":makeQuery(id+"F7.opPattern","COPY",BODY,{"derivedFrom":makeQuery(id+"F2.opExtrude","SWEPT_BODY",BODY,{"disambiguationData":[OSD([sQuery(id+"F0.wireOp",EDGE,"E3.14"),sQuery(id+"F0.wireOp",EDGE,"E6"),sQuery(id+"F0.wireOp",EDGE,"E9")])]}),"instanceName":"1"}),"instanceName":"1"}),"instanceName":"1"});
            var Q42;
            Q42=makeQuery(id+"F10.opPattern","COPY",BODY,{"derivedFrom":makeQuery(id+"F9.opPattern","COPY",BODY,{"derivedFrom":makeQuery(id+"F7.opPattern","COPY",BODY,{"derivedFrom":makeQuery(id+"F2.opExtrude","SWEPT_BODY",BODY,{"disambiguationData":[OSD([sQuery(id+"F0.wireOp",EDGE,"E5.13"),sQuery(id+"F0.wireOp",EDGE,"E6"),sQuery(id+"F0.wireOp",EDGE,"E7"),sQuery(id+"F0.wireOp",EDGE,"E8")])]}),"instanceName":"1"}),"instanceName":"1"}),"instanceName":"1"});
            var Q43;
            Q43=makeQuery(id+"F10.opPattern","COPY",BODY,{"derivedFrom":makeQuery(id+"F9.opPattern","COPY",BODY,{"derivedFrom":makeQuery(id+"F7.opPattern","COPY",BODY,{"derivedFrom":makeQuery(id+"F3.opExtrude","SWEPT_BODY",BODY,{"disambiguationData":[OSD([sQuery(id+"F0.wireOp",EDGE,"E3.14"),sQuery(id+"F0.wireOp",EDGE,"E6"),sQuery(id+"F0.wireOp",EDGE,"E8"),sQuery(id+"F0.wireOp",EDGE,"E9")])]}),"instanceName":"1"}),"instanceName":"1"}),"instanceName":"1"});
            var Q44;
            Q44=makeQuery(id+"F10.opPattern","COPY",BODY,{"derivedFrom":makeQuery(id+"F9.opPattern","COPY",BODY,{"derivedFrom":makeQuery(id+"F8.opPattern","COPY",BODY,{"derivedFrom":makeQuery(id+"F2.opExtrude","SWEPT_BODY",BODY,{"disambiguationData":[OSD([sQuery(id+"F0.wireOp",EDGE,"E3.14"),sQuery(id+"F0.wireOp",EDGE,"E6"),sQuery(id+"F0.wireOp",EDGE,"E9")])]}),"instanceName":"1"}),"instanceName":"1"}),"instanceName":"1"});
            var Q45;
            Q45=makeQuery(id+"F10.opPattern","COPY",BODY,{"derivedFrom":makeQuery(id+"F9.opPattern","COPY",BODY,{"derivedFrom":makeQuery(id+"F8.opPattern","COPY",BODY,{"derivedFrom":makeQuery(id+"F2.opExtrude","SWEPT_BODY",BODY,{"disambiguationData":[OSD([sQuery(id+"F0.wireOp",EDGE,"E5.13"),sQuery(id+"F0.wireOp",EDGE,"E6"),sQuery(id+"F0.wireOp",EDGE,"E7"),sQuery(id+"F0.wireOp",EDGE,"E8")])]}),"instanceName":"1"}),"instanceName":"1"}),"instanceName":"1"});
            var Q46;
            Q46=makeQuery(id+"F10.opPattern","COPY",BODY,{"derivedFrom":makeQuery(id+"F9.opPattern","COPY",BODY,{"derivedFrom":makeQuery(id+"F8.opPattern","COPY",BODY,{"derivedFrom":makeQuery(id+"F3.opExtrude","SWEPT_BODY",BODY,{"disambiguationData":[OSD([sQuery(id+"F0.wireOp",EDGE,"E3.14"),sQuery(id+"F0.wireOp",EDGE,"E6"),sQuery(id+"F0.wireOp",EDGE,"E8"),sQuery(id+"F0.wireOp",EDGE,"E9")])]}),"instanceName":"1"}),"instanceName":"1"}),"instanceName":"1"});
            var Q47;
            Q47=makeQuery(id+"F10.opPattern","COPY",BODY,{"derivedFrom":makeQuery(id+"F9.opPattern","COPY",BODY,{"derivedFrom":makeQuery(id+"F8.opPattern","COPY",BODY,{"derivedFrom":makeQuery(id+"F7.opPattern","COPY",BODY,{"derivedFrom":makeQuery(id+"F2.opExtrude","SWEPT_BODY",BODY,{"disambiguationData":[OSD([sQuery(id+"F0.wireOp",EDGE,"E3.14"),sQuery(id+"F0.wireOp",EDGE,"E6"),sQuery(id+"F0.wireOp",EDGE,"E9")])]}),"instanceName":"1"}),"instanceName":"1"}),"instanceName":"1"}),"instanceName":"1"});
            var Q48;
            Q48=makeQuery(id+"F10.opPattern","COPY",BODY,{"derivedFrom":makeQuery(id+"F9.opPattern","COPY",BODY,{"derivedFrom":makeQuery(id+"F8.opPattern","COPY",BODY,{"derivedFrom":makeQuery(id+"F7.opPattern","COPY",BODY,{"derivedFrom":makeQuery(id+"F2.opExtrude","SWEPT_BODY",BODY,{"disambiguationData":[OSD([sQuery(id+"F0.wireOp",EDGE,"E5.13"),sQuery(id+"F0.wireOp",EDGE,"E6"),sQuery(id+"F0.wireOp",EDGE,"E7"),sQuery(id+"F0.wireOp",EDGE,"E8")])]}),"instanceName":"1"}),"instanceName":"1"}),"instanceName":"1"}),"instanceName":"1"});
            booleanBodies(context, id + "F16", {"operationType" : BooleanOperationType.SUBTRACTION, "tools" : qUnion([Q0, Q1, Q2]), "targets" : qUnion([Q3, Q4, Q5, Q6, Q7, Q8, Q9, Q10, Q11, Q12, Q13, Q14, Q15, Q16, Q17, Q18, Q19, Q20, Q21, Q22, Q23, Q24, Q25, Q26, Q27, Q28, Q29, Q30, Q31, Q32, Q33, Q34, Q35, Q36, Q37, Q38, Q39, Q40, Q41, Q42, Q43, Q44, Q45, Q46, Q47, Q48])});
        }
    });
